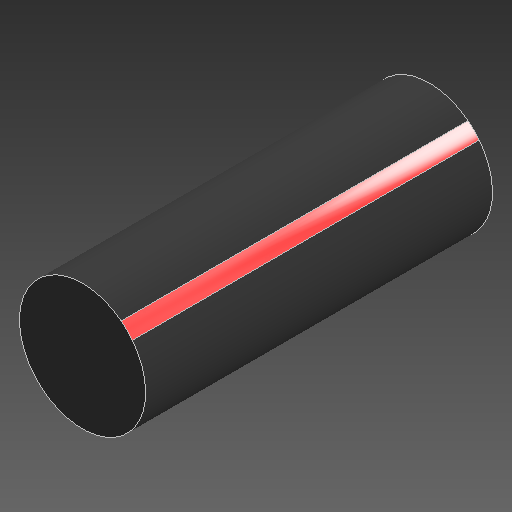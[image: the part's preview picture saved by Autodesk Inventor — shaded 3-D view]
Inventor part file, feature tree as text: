
AUTODESK INVENTOR PART (.ipt)
format: ipt  version: 2020 (Build 240168000, 168)  size: 104,960 bytes
history: native  units: mm
features: other x4, plane x1
ambient origin geometry x8: Origin, YZ Plane, XZ Plane, XY Plane, X Axis, Y Axis, Z Axis, Center Point
bodies: Body1 (feature_tree)
feature tree (5):
  other  "自動販賣機.ipt"
  plane  "工作平面1"
  other  "實體37::自動販賣機.ipt"
  other  "標籤特徵1"
  other  "實體1"
